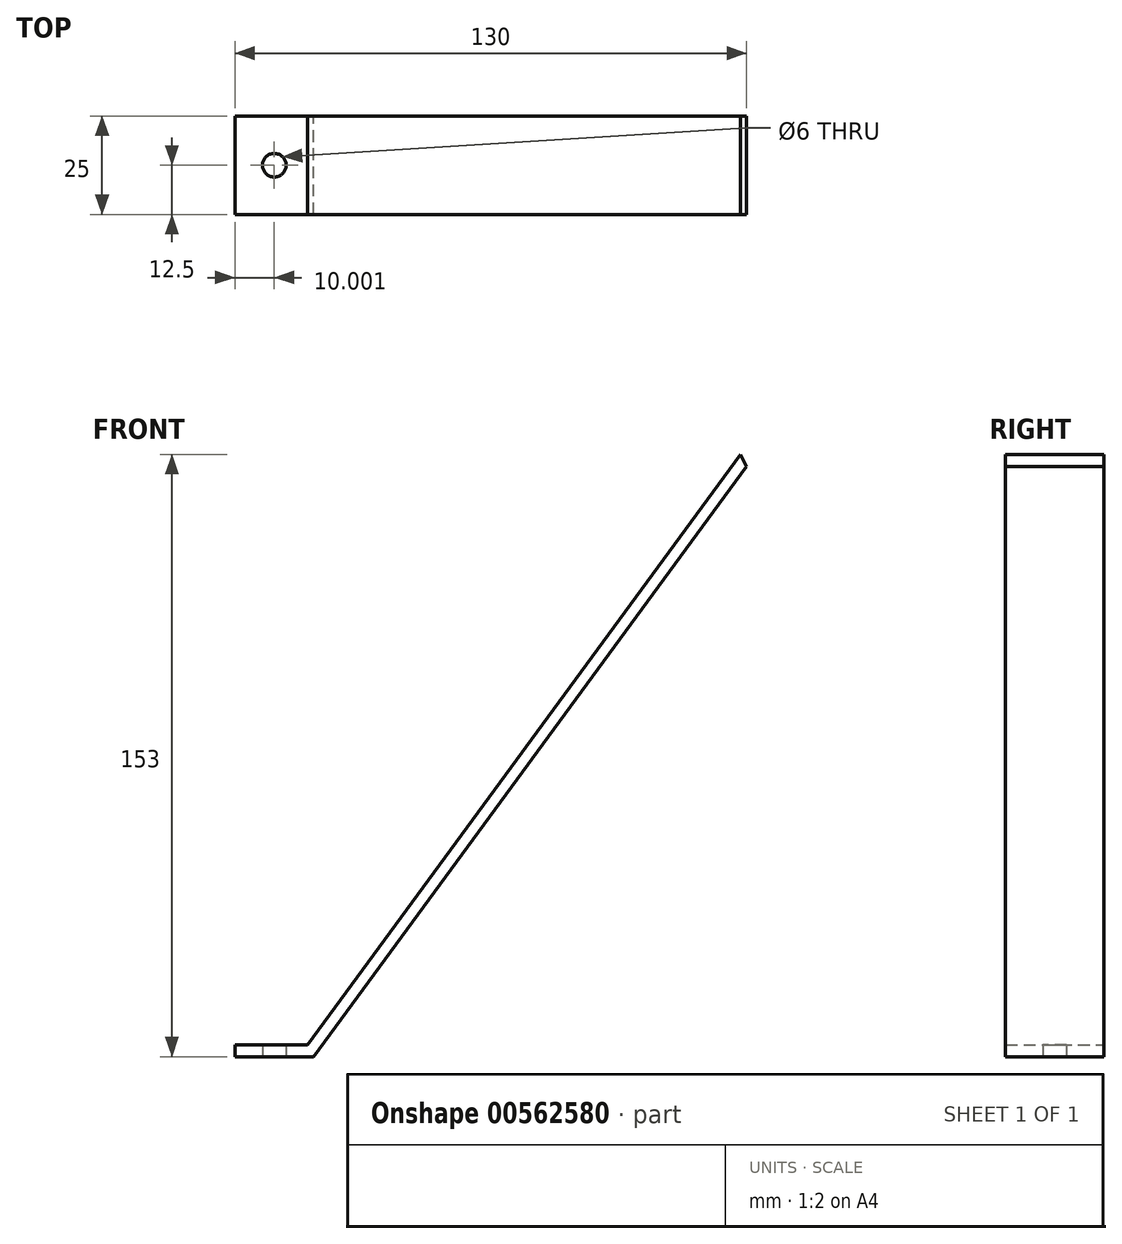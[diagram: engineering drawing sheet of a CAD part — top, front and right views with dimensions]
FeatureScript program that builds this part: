
annotation { "Feature Type Name" : "Feature", "Feature Type Description" : "" }
export const myFeature = defineFeature(function(context is Context, id is Id, definition is map)
    precondition{}
    {
        {
            var Q0;
            Q0=qCreatedBy(makeId("Front.planeOp"),FACE);
            var sketch = newSketch(context, id + "F0", { "sketchPlane" : qUnion([Q0])});
            skLineSegment(sketch, "E0", {"start": v(-58.14, 0) * mm, "end": v(-38.14, 0) * mm});
            skLineSegment(sketch, "E1", {"start": v(-38.14, 0) * mm, "end": v(71.86, 150) * mm});
            skLineSegment(sketch, "E2", {"start": v(-38.14, 0) * mm, "end": v(91.86, 0) * mm});
            skLineSegment(sketch, "E3", {"start": v(91.86, 0) * mm, "end": v(91.86, 150) * mm});
            skLineSegment(sketch, "E4.1", {"start": v(-39.66, 3) * mm, "end": v(70.34, 153) * mm});
            skLineSegment(sketch, "E4.2", {"start": v(-58.14, 3) * mm, "end": v(-39.66, 3) * mm});
            skLineSegment(sketch, "E5", {"start": v(-58.14, 3) * mm, "end": v(-58.14, 0) * mm});
            skLineSegment(sketch, "E6", {"start": v(70.34, 153) * mm, "end": v(71.86, 150) * mm});
            skSolve(sketch);
        }
        {
            var Q0;
            Q0 = qSketchRegion(id + "F0", true);
            extrude(context, id + "F1", {"entities" : qUnion([Q0]), "depth" : 25 * mm, "offsetDistance" : 25 * mm});
        }
        {
            var Q0;
            Q0=qCreatedBy(makeId("Top.planeOp"),FACE);
            var sketch = newSketch(context, id + "F2", { "sketchPlane" : qUnion([Q0])});
            skCircle(sketch, "E7", {"center": v(-48.14, -12.5) * mm, "radius": 3 * mm});
            skSolve(sketch);
        }
        {
            var Q0;
            Q0 = qSketchRegion(id + "F2", true);
            extrude(context, id + "F3", {"entities" : qUnion([Q0]), "operationType" : NewBodyOperationType.REMOVE, "depth" : 25 * mm, "offsetDistance" : 25 * mm});
        }
    });
